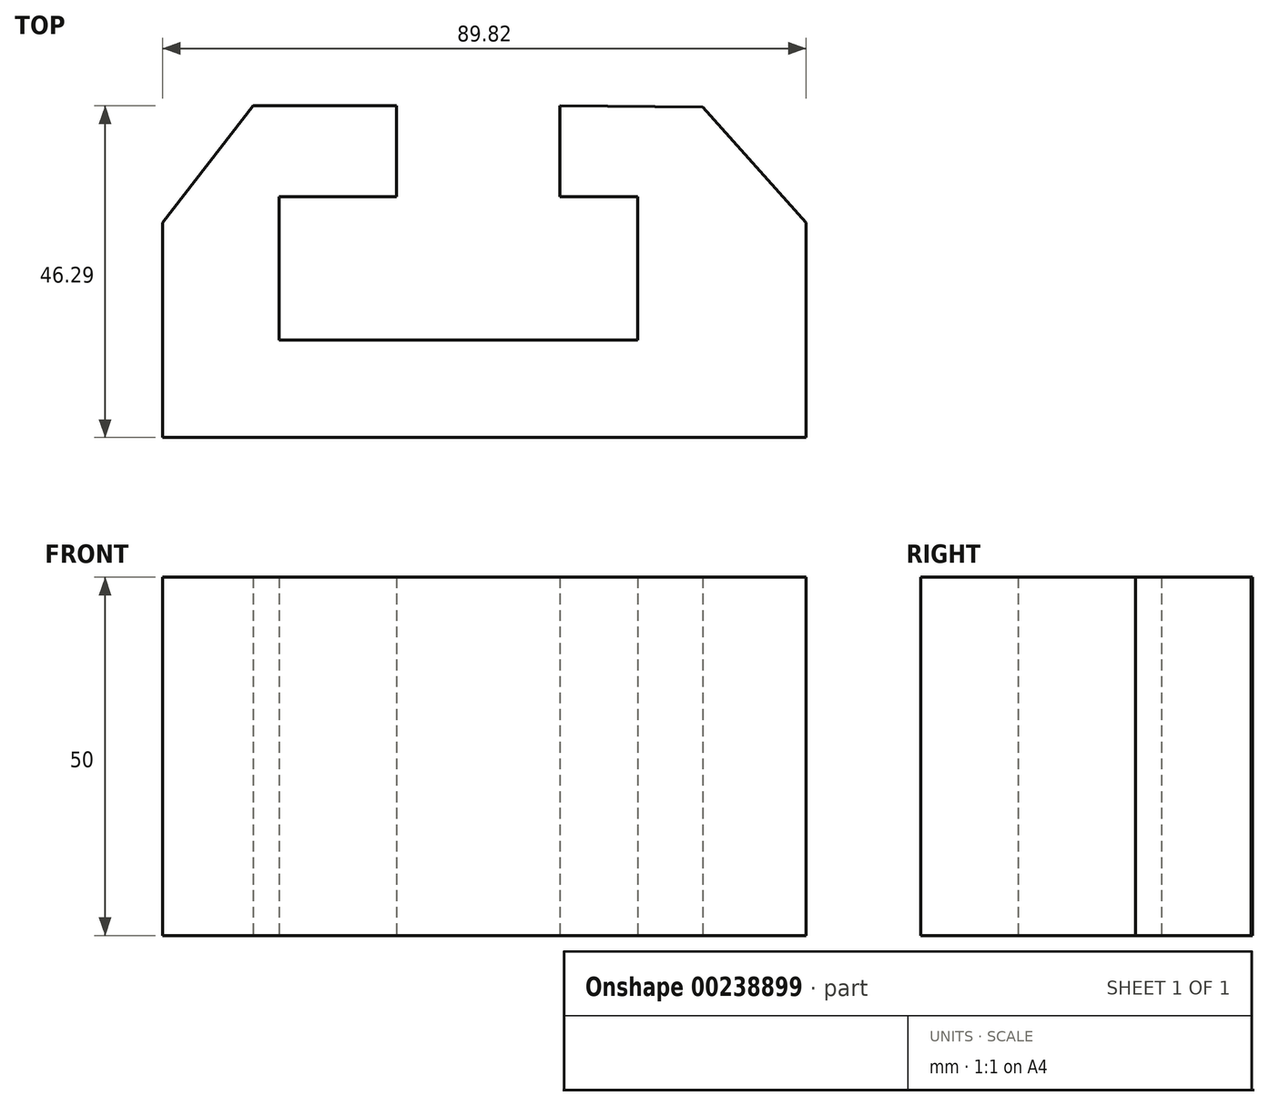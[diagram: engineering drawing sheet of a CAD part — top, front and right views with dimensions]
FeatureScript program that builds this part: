
annotation { "Feature Type Name" : "Feature", "Feature Type Description" : "" }
export const myFeature = defineFeature(function(context is Context, id is Id, definition is map)
    precondition{}
    {
        {
            var Q0;
            Q0=qCreatedBy(makeId("Top.planeOp"),FACE);
            var sketch = newSketch(context, id + "F0", { "sketchPlane" : qUnion([Q0])});
            skLineSegment(sketch, "E0", {"start": v(-49.44, -30) * mm, "end": v(40.38, -30) * mm});
            skLineSegment(sketch, "E1", {"start": v(-49.44, -30) * mm, "end": v(-49.44, 0) * mm});
            skLineSegment(sketch, "E2", {"start": v(40.38, -30) * mm, "end": v(40.38, 0) * mm});
            skLineSegment(sketch, "E3", {"start": v(-49.44, 0) * mm, "end": v(-36.77, 16.29) * mm});
            skLineSegment(sketch, "E4", {"start": v(40.38, 0) * mm, "end": v(26, 16.08) * mm});
            skLineSegment(sketch, "E5", {"start": v(-36.77, 16.29) * mm, "end": v(-16.77, 16.29) * mm});
            skLineSegment(sketch, "E6", {"start": v(-16.77, 16.29) * mm, "end": v(-16.77, 3.62) * mm});
            skLineSegment(sketch, "E7", {"start": v(-16.77, 3.62) * mm, "end": v(-33.15, 3.62) * mm});
            skLineSegment(sketch, "E8", {"start": v(-33.15, 3.62) * mm, "end": v(-33.15, -16.38) * mm});
            skLineSegment(sketch, "E9", {"start": v(-33.15, -16.38) * mm, "end": v(16.85, -16.38) * mm});
            skLineSegment(sketch, "E10", {"start": v(16.85, -16.38) * mm, "end": v(16.85, 3.62) * mm});
            skLineSegment(sketch, "E11", {"start": v(6, 16.29) * mm, "end": v(6, 3.62) * mm});
            skLineSegment(sketch, "E12", {"start": v(6, 16.29) * mm, "end": v(26, 16.08) * mm});
            skLineSegment(sketch, "E13", {"start": v(6, 3.62) * mm, "end": v(16.85, 3.62) * mm});
            skSolve(sketch);
        }
        {
            var Q0;
            Q0 = qSketchRegion(id + "F0", true);
            extrude(context, id + "F1", {"entities" : qUnion([Q0]), "depth" : 25 * mm});
        }
        {
            var Q0;
            Q0=makeQuery(id+"F1.opExtrude","CAP_FACE",FACE,{"disambiguationData":[OSD([sQuery(id+"F0.wireOp",EDGE,"E0"),sQuery(id+"F0.wireOp",EDGE,"E1"),sQuery(id+"F0.wireOp",EDGE,"E2"),sQuery(id+"F0.wireOp",EDGE,"E3"),sQuery(id+"F0.wireOp",EDGE,"E4"),sQuery(id+"F0.wireOp",EDGE,"E5"),sQuery(id+"F0.wireOp",EDGE,"E6"),sQuery(id+"F0.wireOp",EDGE,"E7"),sQuery(id+"F0.wireOp",EDGE,"E8"),sQuery(id+"F0.wireOp",EDGE,"E9"),sQuery(id+"F0.wireOp",EDGE,"E10"),sQuery(id+"F0.wireOp",EDGE,"E11"),sQuery(id+"F0.wireOp",EDGE,"E12"),sQuery(id+"F0.wireOp",EDGE,"E13")])],"isStart":false});
            extrude(context, id + "F2", {"entities" : qUnion([Q0]), "operationType" : NewBodyOperationType.ADD, "depth" : 25 * mm});
        }
    });
